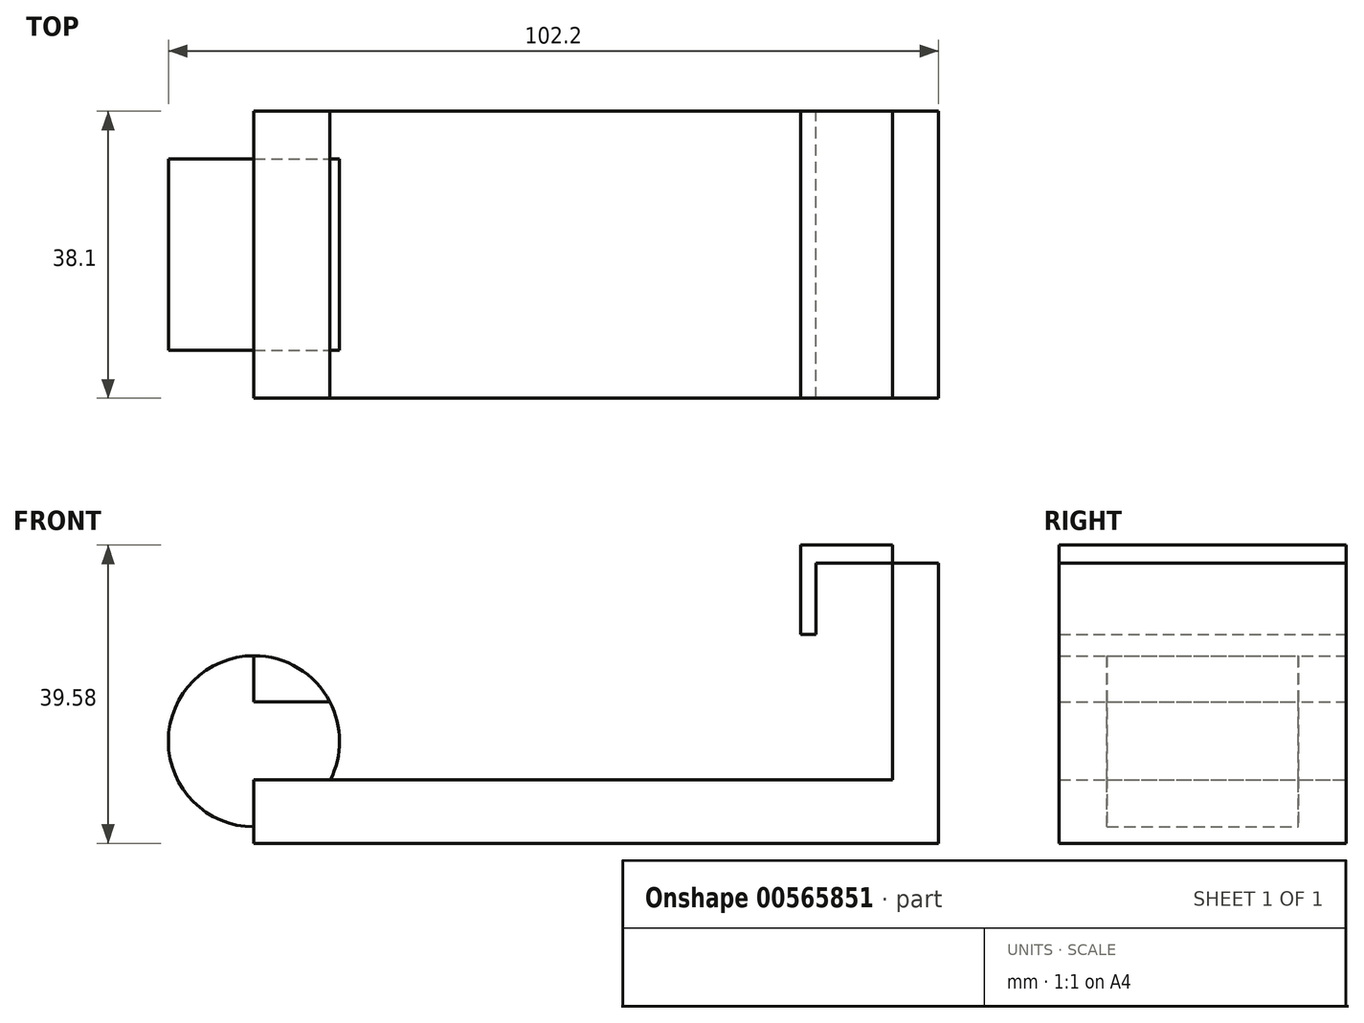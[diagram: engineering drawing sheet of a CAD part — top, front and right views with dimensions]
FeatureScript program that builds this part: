
annotation { "Feature Type Name" : "Feature", "Feature Type Description" : "" }
export const myFeature = defineFeature(function(context is Context, id is Id, definition is map)
    precondition{}
    {
        {
            var Q0;
            Q0=qCreatedBy(makeId("Front.planeOp"),FACE);
            var sketch = newSketch(context, id + "F0", { "sketchPlane" : qUnion([Q0])});
            skLineSegment(sketch, "E0.bottom", {"start": v(-48.21, -8.4) * mm, "end": v(36.54, -8.4) * mm});
            skLineSegment(sketch, "E0.top", {"start": v(-48.21, 0) * mm, "end": v(36.54, 0) * mm});
            skLineSegment(sketch, "E0.left", {"start": v(-48.21, -8.4) * mm, "end": v(-48.21, 0) * mm});
            skLineSegment(sketch, "E0.right", {"start": v(36.54, -8.4) * mm, "end": v(36.54, 0) * mm});
            skLineSegment(sketch, "E1.bottom", {"start": v(-48.21, 10.37) * mm, "end": v(36.54, 10.37) * mm});
            skLineSegment(sketch, "E1.top", {"start": v(-48.21, 19.32) * mm, "end": v(36.54, 19.32) * mm});
            skLineSegment(sketch, "E1.left", {"start": v(-48.21, 10.37) * mm, "end": v(-48.21, 19.32) * mm});
            skLineSegment(sketch, "E1.right", {"start": v(36.54, 10.37) * mm, "end": v(36.54, 19.32) * mm});
            skCircle(sketch, "E2", {"center": v(-48.21, 5.14) * mm, "radius": 11.36 * mm});
            skLineSegment(sketch, "E3.bottom", {"start": v(36.54, -8.4) * mm, "end": v(42.63, -8.4) * mm});
            skLineSegment(sketch, "E3.top", {"start": v(36.54, 31.18) * mm, "end": v(42.63, 31.18) * mm});
            skLineSegment(sketch, "E3.left", {"start": v(36.54, -8.4) * mm, "end": v(36.54, 31.18) * mm});
            skLineSegment(sketch, "E3.right", {"start": v(42.63, -8.4) * mm, "end": v(42.63, 31.18) * mm});
            skLineSegment(sketch, "E4.bottom", {"start": v(42.63, 31.18) * mm, "end": v(26.39, 31.18) * mm});
            skLineSegment(sketch, "E4.top", {"start": v(42.63, 28.79) * mm, "end": v(26.39, 28.79) * mm});
            skLineSegment(sketch, "E4.left", {"start": v(42.63, 31.18) * mm, "end": v(42.63, 28.79) * mm});
            skLineSegment(sketch, "E4.right", {"start": v(26.39, 31.18) * mm, "end": v(26.39, 28.79) * mm});
            skLineSegment(sketch, "E5.bottom", {"start": v(26.39, 31.18) * mm, "end": v(24.36, 31.18) * mm});
            skLineSegment(sketch, "E5.top", {"start": v(26.39, 19.32) * mm, "end": v(24.36, 19.32) * mm});
            skLineSegment(sketch, "E5.left", {"start": v(26.39, 31.18) * mm, "end": v(26.39, 19.32) * mm});
            skLineSegment(sketch, "E5.right", {"start": v(24.36, 31.18) * mm, "end": v(24.36, 19.32) * mm});
            skPoint(sketch, "E6.oppositeSnap0", {"position": v(26.39, 25.25) * mm});
            skLineSegment(sketch, "E6.bottom", {"start": v(35.02, 19.32) * mm, "end": v(29.94, 19.32) * mm});
            skLineSegment(sketch, "E6.top", {"start": v(35.02, 25.25) * mm, "end": v(29.94, 25.25) * mm});
            skLineSegment(sketch, "E6.left", {"start": v(35.02, 19.32) * mm, "end": v(35.02, 25.25) * mm});
            skLineSegment(sketch, "E6.right", {"start": v(29.94, 19.32) * mm, "end": v(29.94, 25.25) * mm});
            skSolve(sketch);
        }
        {
            var Q0;
            {var subQ6=sQuery(id+"F0.wireOp",EDGE,"E0.left");var subQ7=sQuery(id+"F0.wireOp",EDGE,"E0.top");var subQ8=makeQuery(id+"F0.imprint","INTERSECT",VERTEX,{"derivedFrom":[subQ7,subQ6]});Q0=makeQuery(id+"F0.imprint","IMPRINT",FACE,{"disambiguationData":[TD([[makeQuery(id+"F0.imprint","IMPRINT",EDGE,{"disambiguationData":[TD([[subQ8,-1.0]])],"derivedFrom":subQ7}),1.0]])]});}
            extrude(context, id + "F1", {"entities" : qUnion([Q0]), "endBound" : BoundingType.SYMMETRIC, "depth" : 25.4 * mm, "offsetDistance" : 25.4 * mm});
        }
        {
            var Q0;
            {var subQ5=sQuery(id+"F0.wireOp",EDGE,"E0.bottom");Q0=makeQuery(id+"F0.imprint","IMPRINT",FACE,{"disambiguationData":[TD([[makeQuery(id+"F0.imprint","IMPRINT",EDGE,{"derivedFrom":subQ5}),1.0]])]});}
            var Q1;
            {var subQ4=sQuery(id+"F0.wireOp",EDGE,"E3.bottom");Q1=makeQuery(id+"F0.imprint","IMPRINT",FACE,{"disambiguationData":[TD([[makeQuery(id+"F0.imprint","IMPRINT",EDGE,{"derivedFrom":subQ4}),1.0]])]});}
            var Q2;
            {var subQ0=sQuery(id+"F0.wireOp",EDGE,"E4.bottom");var subQ1=sQuery(id+"F0.wireOp",EDGE,"E3.left");var subQ2=makeQuery(id+"F0.imprint","INTERSECT",VERTEX,{"derivedFrom":[subQ1,subQ0]});Q2=makeQuery(id+"F0.imprint","IMPRINT",FACE,{"disambiguationData":[TD([[makeQuery(id+"F0.imprint","IMPRINT",EDGE,{"disambiguationData":[TD([[subQ2,1.0]])],"derivedFrom":subQ1}),1.0]])]});}
            var Q3;
            {var subQ5=sQuery(id+"F0.wireOp",EDGE,"E4.left");Q3=makeQuery(id+"F0.imprint","IMPRINT",FACE,{"disambiguationData":[TD([[makeQuery(id+"F0.imprint","IMPRINT",EDGE,{"derivedFrom":subQ5}),-1.0]])]});}
            var Q4;
            {var subQ3=sQuery(id+"F0.wireOp",EDGE,"E5.bottom");Q4=makeQuery(id+"F0.imprint","IMPRINT",FACE,{"disambiguationData":[TD([[makeQuery(id+"F0.imprint","IMPRINT",EDGE,{"derivedFrom":subQ3}),1.0]])]});}
            var Q5;
            {var subQ0=sQuery(id+"F0.wireOp",EDGE,"E0.left");var subQ1=sQuery(id+"F0.wireOp",EDGE,"E0.top");var subQ2=makeQuery(id+"F0.imprint","INTERSECT",VERTEX,{"derivedFrom":[subQ1,subQ0]});Q5=makeQuery(id+"F0.imprint","IMPRINT",FACE,{"disambiguationData":[TD([[makeQuery(id+"F0.imprint","IMPRINT",EDGE,{"disambiguationData":[TD([[subQ2,-1.0]])],"derivedFrom":subQ1}),-1.0]])]});}
            extrude(context, id + "F2", {"entities" : qUnion([Q0, Q1, Q2, Q3, Q4, Q5]), "operationType" : NewBodyOperationType.ADD, "endBound" : BoundingType.SYMMETRIC, "depth" : 38.1 * mm, "offsetDistance" : 25.4 * mm});
        }
        {
            var Q0;
            {var subQ4=sQuery(id+"F0.wireOp",EDGE,"E5.top");Q0=makeQuery(id+"F0.imprint","IMPRINT",FACE,{"disambiguationData":[TD([[makeQuery(id+"F0.imprint","IMPRINT",EDGE,{"derivedFrom":subQ4}),1.0]])]});}
            var Q1;
            Q1=makeQuery(id+"F0.imprint","IMPRINT",FACE,{"disambiguationData":[TD([[makeQuery(id+"F0.imprint","IMPRINT",EDGE,{"derivedFrom":sQuery(id+"F0.wireOp",EDGE,"E6.bottom")}),-1.0]])]});
            var Q2;
            {var subQ0=sQuery(id+"F0.wireOp",EDGE,"E1.left");var subQ1=sQuery(id+"F0.wireOp",EDGE,"E1.bottom");var subQ2=makeQuery(id+"F0.imprint","INTERSECT",VERTEX,{"derivedFrom":[subQ1,subQ0]});Q2=makeQuery(id+"F0.imprint","IMPRINT",FACE,{"disambiguationData":[TD([[makeQuery(id+"F0.imprint","IMPRINT",EDGE,{"disambiguationData":[TD([[subQ2,-1.0]])],"derivedFrom":subQ1}),1.0]])]});}
            extrude(context, id + "F3", {"entities" : qUnion([Q0, Q1, Q2]), "endBound" : BoundingType.SYMMETRIC, "depth" : 38.1 * mm, "offsetDistance" : 25.4 * mm});
        }
    });
